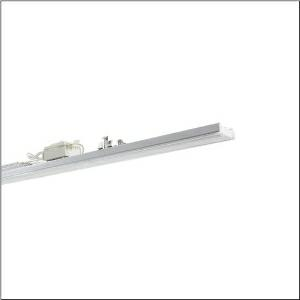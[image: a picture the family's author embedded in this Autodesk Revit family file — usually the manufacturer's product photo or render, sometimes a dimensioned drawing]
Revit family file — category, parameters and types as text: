
# Revit family: licross_r__21_recessed_mo_52tl1e7n485g_8290
name_source: partatom
category: Lighting Fixtures
units: mm (PartAtom-declared; Revit-internal decimal feet)

## family parameters
Cut with Voids When Loaded = No
Host = Face
Light Source = No
Part Type = Normal
Room Calculation Point = No
Round Connector Dimension = Use Diameter
Shared = No

## types (1)
- Licross® 21 Recessed MO (1 x LED, 8530 lm, 47.9 W, 4000K)
    Apparent Load = 48 VA
    CIE Flux Codes = 85 95 99 100 100
    Color Rendering = 80
    Color Temperature = 4000K
    Default Elevation = 1800 mm
    Description = Licross® 21 Recessed MO, luminaire insert, of sheet steel, galvanised, coil coated, white, length: 1.500mm, width: 66mm, height: 67mm, LED rated luminous flux: 8.530lm, light colour: 840, control gear: ON/OFF, with plug, 3-pole, with phase selection, mains connection: 220..240V, AC, 50/60Hz, rated input power: 48W, internal wiring halogen-free, primary light control with lens, of plastic, primary optical cover: cover, of PMMA, light emission: direct distribution, primary light characteristic: symmetric, protection rating (complete): IP40, insulation class (complete): insulation class I (protective earthing), certification: CE, ENEC, VDE, UKCA, protection symbol: D if used in an environment without relevant dust loads with corresponding accessories, impact resistance: IK06, permissible ambient temperature for indoor applications: -35..+40°C, corresponds to IFS (International Featured Standards) requirements for safety and quality in the food industry, reducing of maximum allowable ambient temperature of 5°C with ceiling mounting, LABS conformity tested according to VDMA 24364:2018-05, packaging unit: 1 piece
    Height = 58 mm
    Lamp = 1 x LED
    Lamp Light Flux = 8530 lm
    Lamp Power = 47.9 W
    Lamp count = 1
    Length = 1500 mm
    Luminous efficacy = 178 lm/W
    Manufacturer = Siteco
    ModVariant = No
    Model = 52TL1E7N485G
    Mounting Place = Ceiling
    Mounting Type = Pendant
    Number of Poles = 1
    OnlyDefault = Yes
    Power Factor = 1
    Product Name = Licross® 21 Recessed MO
    Product group = luminaire insert | ceiling pendant
    ProductGroupID = 902
    Protection Class = Protection class I
    Protection Degree = IP 40
    RLX_Detail_Level = 1
    RLX_Emergency_Light_Flux = 0 lm
    RLX_Emergency_Type = 0
    RLX_Emergency_Type_DB = No
    RlxData = <blob elided: 21041 chars, md5=94829b50>
    Socket = socket
    Standby Power = 0 W
    System Light Flux = 8530 lm
    System Power = 48 W
    Type Comments = Product without accessories
    Type Image = l_1296930.jpg
    URL = http://relux.com
    VarID = ---
    Voltage = 0 V
    Weight = 0.00 kg
    Width = 66 mm

## geometry (parser evidence)
native form markers: Blend x4, Sweep x10
no freeform markers — native parametric forms only
